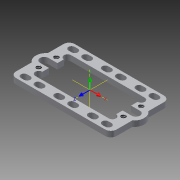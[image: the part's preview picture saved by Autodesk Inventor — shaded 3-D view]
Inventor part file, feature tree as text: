
AUTODESK INVENTOR PART (.ipt)
format: ipt  version: 2015 (Build 190159000, 159)  size: 321,024 bytes
history: native  units: in
note: dims shown in document units (in); Inventor stores cm internally (conversion verified against a paired STEP export)
features: hole x19, sketch x11, other x9, extrude x1, imported_body x1, projected_geometry x1
ambient origin geometry x8: Origin, YZ Plane, XZ Plane, XY Plane, X Axis, Y Axis, Z Axis, Center Point
bodies: Solid1 (feature_tree)
feature tree (42):
  other  "User Library-575112.sat1"
  other  "UCS1"
  sketch  "Sketch2"  dims[d0=0.0in d1=0.063in d2=0.0in d3=0.0in d4=0.0in d5=0.0in d6=1.0in d7=0.0in]
  sketch  "Sketch3"  dims[d8=0.104in d9=0.276in d10=0.375in d11=0.25in d12=0.5635in d13=0.432in d14=0.8108in]
  extrude  "Extrusion1"  Depth=1.0in TaperAngle=0.0deg
  hole  "Hole1"  [1 undecoded]
  hole  "Hole3"  [1 undecoded]
  hole  "Hole5"  [1 undecoded]
  hole  "Hole7"  [1 undecoded]
  hole  "Hole9"  [1 undecoded]
  hole  "Hole11"  [1 undecoded]
  hole  "Hole13"  [1 undecoded]
  hole  "Hole15"  [1 undecoded]
  hole  "Hole17"  [1 undecoded]
  hole  "Hole19"  [1 undecoded]
  imported_body  "Base1"
  projected_geometry  "Projected Loop2"
  sketch  "Sketch4"  dims[d15=0.104in d16=0.2831in d17=0.375in d18=0.25in d19=0.5635in d20=0.3521in d21=120.0deg]
  hole  "Hole2"  [1 undecoded]
  sketch  "Sketch5"  dims[d22=0.104in d23=0.2831in d24=0.375in d25=0.25in d26=0.5635in d27=0.3521in d28=120.0deg]
  hole  "Hole4"  [1 undecoded]
  sketch  "Sketch6"  dims[d29=0.104in d30=0.2831in d31=0.375in d32=0.25in d33=0.5635in d34=0.3521in d35=120.0deg]
  hole  "Hole6"  [1 undecoded]
  sketch  "Sketch7"  dims[d36=0.104in d37=0.2831in d38=0.375in d39=0.25in d40=0.5635in d41=0.3521in d42=120.0deg]
  hole  "Hole8"  [1 undecoded]
  sketch  "Sketch8"  dims[d43=0.104in d44=0.2831in d45=0.375in d46=0.25in d47=0.5635in d48=0.3521in d49=120.0deg]
  hole  "Hole10"  [1 undecoded]
  sketch  "Sketch9"  dims[d50=0.104in d51=0.138in d52=0.375in d53=0.25in d54=0.5635in d55=0.207in d56=120.0deg]
  hole  "Hole12"  [1 undecoded]
  sketch  "Sketch10"  dims[d57=0.104in d58=0.2831in d59=0.375in d60=0.25in d61=0.5635in d62=0.3521in d63=120.0deg]
  hole  "Hole14"  [1 undecoded]
  sketch  "Sketch11"  dims[d64=0.104in d65=0.2831in d66=0.375in d67=0.25in d68=0.5635in d69=0.3521in d70=120.0deg]
  hole  "Hole16"  [1 undecoded]
  sketch  "Sketch12"  dims[d71=0.104in d72=0.2831in d73=0.375in d74=0.25in d75=0.5635in d76=0.3521in d77=120.0deg]
  hole  "Hole18"  [1 undecoded]
  other  "UCS1: YZ Plane"
  other  "UCS1: XZ Plane"
  other  "UCS1: XY Plane"
  other  "UCS1: X Axis"
  other  "UCS1: Y Axis"
  other  "UCS1: Z Axis"
  other  "UCS1: Center Point"
note: 19 required parameter values undecoded (feature->parameter linkage not recoverable at this tier; creation-order binding heuristic only, values carry confidence <= 0.55)
